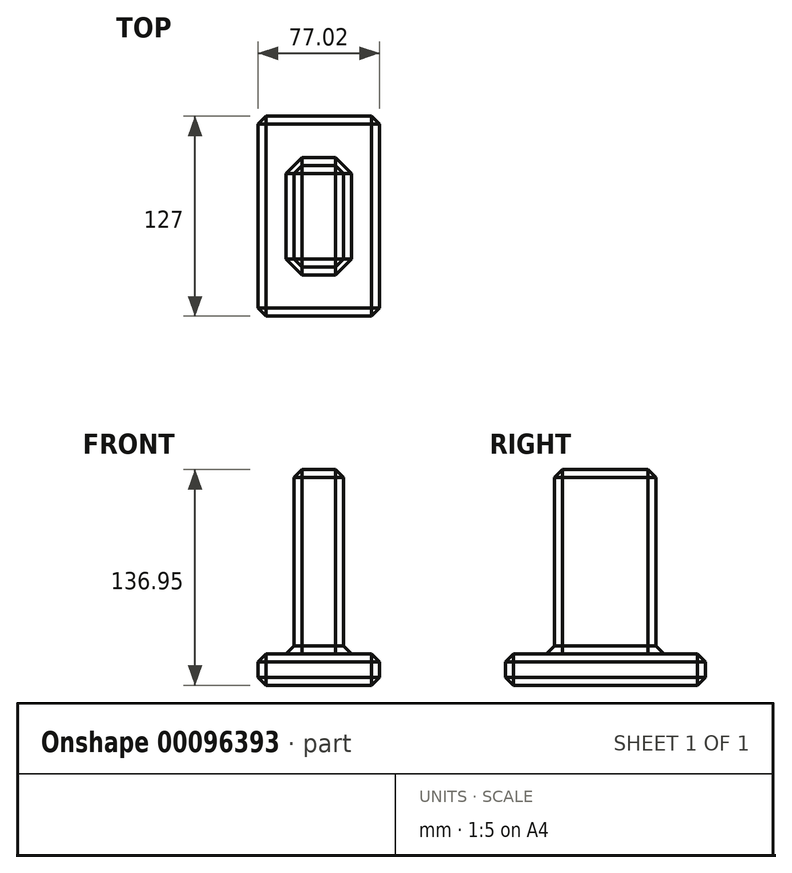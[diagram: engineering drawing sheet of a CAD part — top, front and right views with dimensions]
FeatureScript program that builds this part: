
annotation { "Feature Type Name" : "Feature", "Feature Type Description" : "" }
export const myFeature = defineFeature(function(context is Context, id is Id, definition is map)
    precondition{}
    {
        {
            var Q0;
            Q0=qCreatedBy(makeId("Front.planeOp"),FACE);
            var sketch = newSketch(context, id + "F0", { "sketchPlane" : qUnion([Q0])});
            skLineSegment(sketch, "E0.bottom", {"start": v(-38.5, 9.95) * mm, "end": v(38.5, 9.95) * mm});
            skLineSegment(sketch, "E0.top", {"start": v(-38.5, -9.95) * mm, "end": v(38.5, -9.95) * mm});
            skLineSegment(sketch, "E0.left", {"start": v(-38.5, 9.95) * mm, "end": v(-38.5, -9.95) * mm});
            skLineSegment(sketch, "E0.right", {"start": v(38.5, 9.95) * mm, "end": v(38.5, -9.95) * mm});
            skPoint(sketch, "E0.middle", {"position": v(0, 0) * mm});
            skSolve(sketch);
        }
        {
            var Q0;
            Q0=makeQuery(id+"F0.imprint","IMPRINT",FACE,{"disambiguationData":[TD([[makeQuery(id+"F0.imprint","IMPRINT",EDGE,{"derivedFrom":sQuery(id+"F0.wireOp",EDGE,"E0.bottom")}),-1.0]])]});
            extrude(context, id + "F1", {"entities" : qUnion([Q0]), "endBound" : BoundingType.SYMMETRIC, "depth" : 127 * mm});
        }
        {
            var Q0;
            Q0=qCreatedBy(makeId("Top.planeOp"),FACE);
            var sketch = newSketch(context, id + "F2", { "sketchPlane" : qUnion([Q0])});
            skLineSegment(sketch, "E1.bottom", {"start": v(-15.7, 32.28) * mm, "end": v(15.7, 32.28) * mm});
            skLineSegment(sketch, "E1.top", {"start": v(-15.7, -32.28) * mm, "end": v(15.7, -32.28) * mm});
            skLineSegment(sketch, "E1.left", {"start": v(-15.7, 32.28) * mm, "end": v(-15.7, -32.28) * mm});
            skLineSegment(sketch, "E1.right", {"start": v(15.7, 32.28) * mm, "end": v(15.7, -32.28) * mm});
            skPoint(sketch, "E1.middle", {"position": v(0, 0) * mm});
            skSolve(sketch);
        }
        {
            var Q0;
            Q0 = qSketchRegion(id + "F2", true);
            extrude(context, id + "F3", {"entities" : qUnion([Q0]), "operationType" : NewBodyOperationType.ADD, "depth" : 127 * mm});
        }
        {
            var Q0;
            Q0=makeQuery(id+"F3.opExtrude","CAP_EDGE",EDGE,{"disambiguationData":[OSD([sQuery(id+"F2.wireOp",EDGE,"E1.top")])],"isStart":false});
            var Q1;
            Q1=makeQuery(id+"F3.opExtrude","SWEPT_EDGE",EDGE,{"disambiguationData":[OSD([sQuery(id+"F2.wireOp",EDGE,"E1.top"),sQuery(id+"F2.wireOp",EDGE,"E1.right")])]});
            var Q2;
            Q2=makeQuery(id+"F3.opExtrude","CAP_EDGE",EDGE,{"disambiguationData":[OSD([sQuery(id+"F2.wireOp",EDGE,"E1.bottom")])],"isStart":false});
            var Q3;
            Q3=makeQuery(id+"F3.opExtrude","CAP_EDGE",EDGE,{"disambiguationData":[OSD([sQuery(id+"F2.wireOp",EDGE,"E1.right")])],"isStart":false});
            var Q4;
            Q4=makeQuery(id+"F3.opExtrude","CAP_EDGE",EDGE,{"disambiguationData":[OSD([sQuery(id+"F2.wireOp",EDGE,"E1.left")])],"isStart":false});
            var Q5;
            Q5=makeQuery(id+"F3.opExtrude","SWEPT_EDGE",EDGE,{"disambiguationData":[OSD([sQuery(id+"F2.wireOp",EDGE,"E1.bottom"),sQuery(id+"F2.wireOp",EDGE,"E1.right")])]});
            var Q6;
            Q6=makeQuery(id+"F3.opExtrude","SWEPT_EDGE",EDGE,{"disambiguationData":[OSD([sQuery(id+"F2.wireOp",EDGE,"E1.bottom"),sQuery(id+"F2.wireOp",EDGE,"E1.left")])]});
            var Q7;
            Q7=makeQuery(id+"F3.opExtrude","SWEPT_EDGE",EDGE,{"disambiguationData":[OSD([sQuery(id+"F2.wireOp",EDGE,"E1.top"),sQuery(id+"F2.wireOp",EDGE,"E1.left")])]});
            var Q8;
            Q8=makeQuery(id+"F3.boolean.opBoolean","INTERSECT",EDGE,{"derivedFrom":[makeQuery(id+"F1.opExtrude","SWEPT_FACE",FACE,{"disambiguationData":[OSD([sQuery(id+"F0.wireOp",EDGE,"E0.bottom")])]}),makeQuery(id+"F3.opExtrude","SWEPT_FACE",FACE,{"disambiguationData":[OSD([sQuery(id+"F2.wireOp",EDGE,"E1.right")])]})]});
            var Q9;
            Q9=makeQuery(id+"F1.opExtrude","SWEPT_EDGE",EDGE,{"disambiguationData":[OSD([sQuery(id+"F0.wireOp",EDGE,"E0.bottom"),sQuery(id+"F0.wireOp",EDGE,"E0.right")])]});
            var Q10;
            Q10=makeQuery(id+"F1.opExtrude","CAP_EDGE",EDGE,{"disambiguationData":[OSD([sQuery(id+"F0.wireOp",EDGE,"E0.bottom")])],"isStart":false});
            var Q11;
            Q11=makeQuery(id+"F1.opExtrude","CAP_EDGE",EDGE,{"disambiguationData":[OSD([sQuery(id+"F0.wireOp",EDGE,"E0.bottom")])],"isStart":true});
            var Q12;
            Q12=makeQuery(id+"F1.opExtrude","SWEPT_EDGE",EDGE,{"disambiguationData":[OSD([sQuery(id+"F0.wireOp",EDGE,"E0.bottom"),sQuery(id+"F0.wireOp",EDGE,"E0.left")])]});
            var Q13;
            Q13=makeQuery(id+"F1.opExtrude","CAP_EDGE",EDGE,{"disambiguationData":[OSD([sQuery(id+"F0.wireOp",EDGE,"E0.top")])],"isStart":false});
            var Q14;
            Q14=makeQuery(id+"F1.opExtrude","SWEPT_EDGE",EDGE,{"disambiguationData":[OSD([sQuery(id+"F0.wireOp",EDGE,"E0.top"),sQuery(id+"F0.wireOp",EDGE,"E0.left")])]});
            var Q15;
            Q15=makeQuery(id+"F1.opExtrude","CAP_EDGE",EDGE,{"disambiguationData":[OSD([sQuery(id+"F0.wireOp",EDGE,"E0.top")])],"isStart":true});
            var Q16;
            Q16=makeQuery(id+"F1.opExtrude","SWEPT_EDGE",EDGE,{"disambiguationData":[OSD([sQuery(id+"F0.wireOp",EDGE,"E0.top"),sQuery(id+"F0.wireOp",EDGE,"E0.right")])]});
            var Q17;
            Q17=makeQuery(id+"F1.opExtrude","CAP_EDGE",EDGE,{"disambiguationData":[OSD([sQuery(id+"F0.wireOp",EDGE,"E0.right")])],"isStart":true});
            var Q18;
            Q18=makeQuery(id+"F1.opExtrude","CAP_EDGE",EDGE,{"disambiguationData":[OSD([sQuery(id+"F0.wireOp",EDGE,"E0.left")])],"isStart":true});
            var Q19;
            Q19=makeQuery(id+"F1.opExtrude","CAP_EDGE",EDGE,{"disambiguationData":[OSD([sQuery(id+"F0.wireOp",EDGE,"E0.right")])],"isStart":false});
            var Q20;
            Q20=makeQuery(id+"F1.opExtrude","CAP_EDGE",EDGE,{"disambiguationData":[OSD([sQuery(id+"F0.wireOp",EDGE,"E0.left")])],"isStart":false});
            chamfer(context, id + "F4", {"entities" : qUnion([Q0, Q1, Q2, Q3, Q4, Q5, Q6, Q7, Q8, Q9, Q10, Q11, Q12, Q13, Q14, Q15, Q16, Q17, Q18, Q19, Q20]), "chamferType" : ChamferType.TWO_OFFSETS, "width1" : 5.08 * mm, "oppositeDirection" : false, "width2" : 5.08 * mm, "tangentPropagation" : true});
        }
        {
            var Q0;
            Q0=qCreatedBy(makeId("Top.planeOp"),FACE);
            var sketch = newSketch(context, id + "F5", { "sketchPlane" : qUnion([Q0])});
            skLineSegment(sketch, "E2.bottom", {"start": v(-28.8, -31.63) * mm, "end": v(28.8, -31.63) * mm});
            skLineSegment(sketch, "E2.top", {"start": v(-28.8, 31.63) * mm, "end": v(28.8, 31.63) * mm});
            skLineSegment(sketch, "E2.left", {"start": v(-28.8, -31.63) * mm, "end": v(-28.8, 31.63) * mm});
            skLineSegment(sketch, "E2.right", {"start": v(28.8, -31.63) * mm, "end": v(28.8, 31.63) * mm});
            skPoint(sketch, "E2.middle", {"position": v(0, 0) * mm});
            skSolve(sketch);
        }
        {
            var Q0;
            Q0=sQuery(id+"F5.wireOp",EDGE,"E2.left");
            var Q1;
            Q1=sQuery(id+"F5.wireOp",EDGE,"E2.bottom");
            var Q2;
            Q2=sQuery(id+"F5.wireOp",EDGE,"E2.right");
            var Q3;
            Q3=sQuery(id+"F5.wireOp",EDGE,"E2.top");
            extrude(context, id + "F6", {"bodyType" : ToolBodyType.SURFACE, "surfaceEntities" : qUnion([Q0, Q1, Q2, Q3]), "endBound" : BoundingType.SYMMETRIC, "depth" : 254 * mm});
        }
    });
